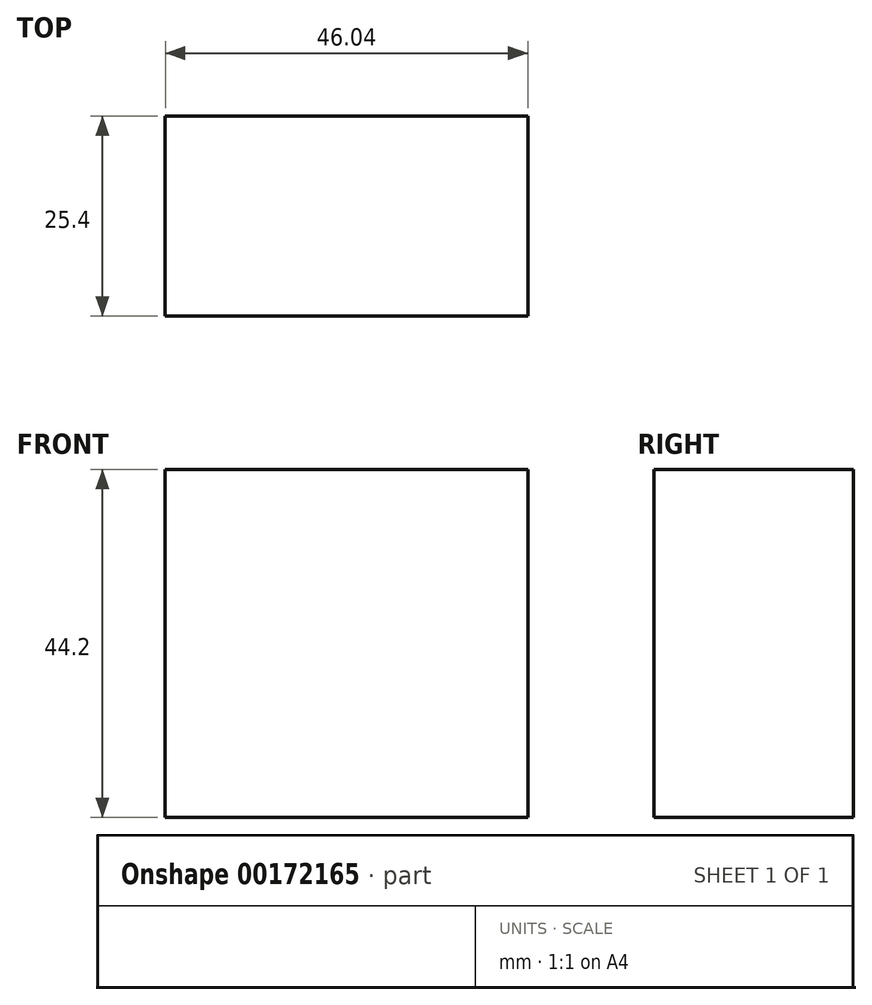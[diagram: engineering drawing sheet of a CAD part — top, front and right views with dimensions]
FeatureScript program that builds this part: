
annotation { "Feature Type Name" : "Feature", "Feature Type Description" : "" }
export const myFeature = defineFeature(function(context is Context, id is Id, definition is map)
    precondition{}
    {
        {
            var Q0;
            Q0=qCreatedBy(makeId("Front.planeOp"),FACE);
            var sketch = newSketch(context, id + "F0", { "sketchPlane" : qUnion([Q0])});
            skLineSegment(sketch, "E0.bottom", {"start": v(0, 0) * mm, "end": v(-46.04, 0) * mm});
            skLineSegment(sketch, "E0.top", {"start": v(0, 44.2) * mm, "end": v(-46.04, 44.2) * mm});
            skLineSegment(sketch, "E0.left", {"start": v(0, 0) * mm, "end": v(0, 44.2) * mm});
            skLineSegment(sketch, "E0.right", {"start": v(-46.04, 0) * mm, "end": v(-46.04, 44.2) * mm});
            skSolve(sketch);
        }
        {
            var Q0;
            Q0 = qSketchRegion(id + "F0", true);
            extrude(context, id + "F1", {"entities" : qUnion([Q0]), "depth" : 25.4 * mm});
        }
    });
